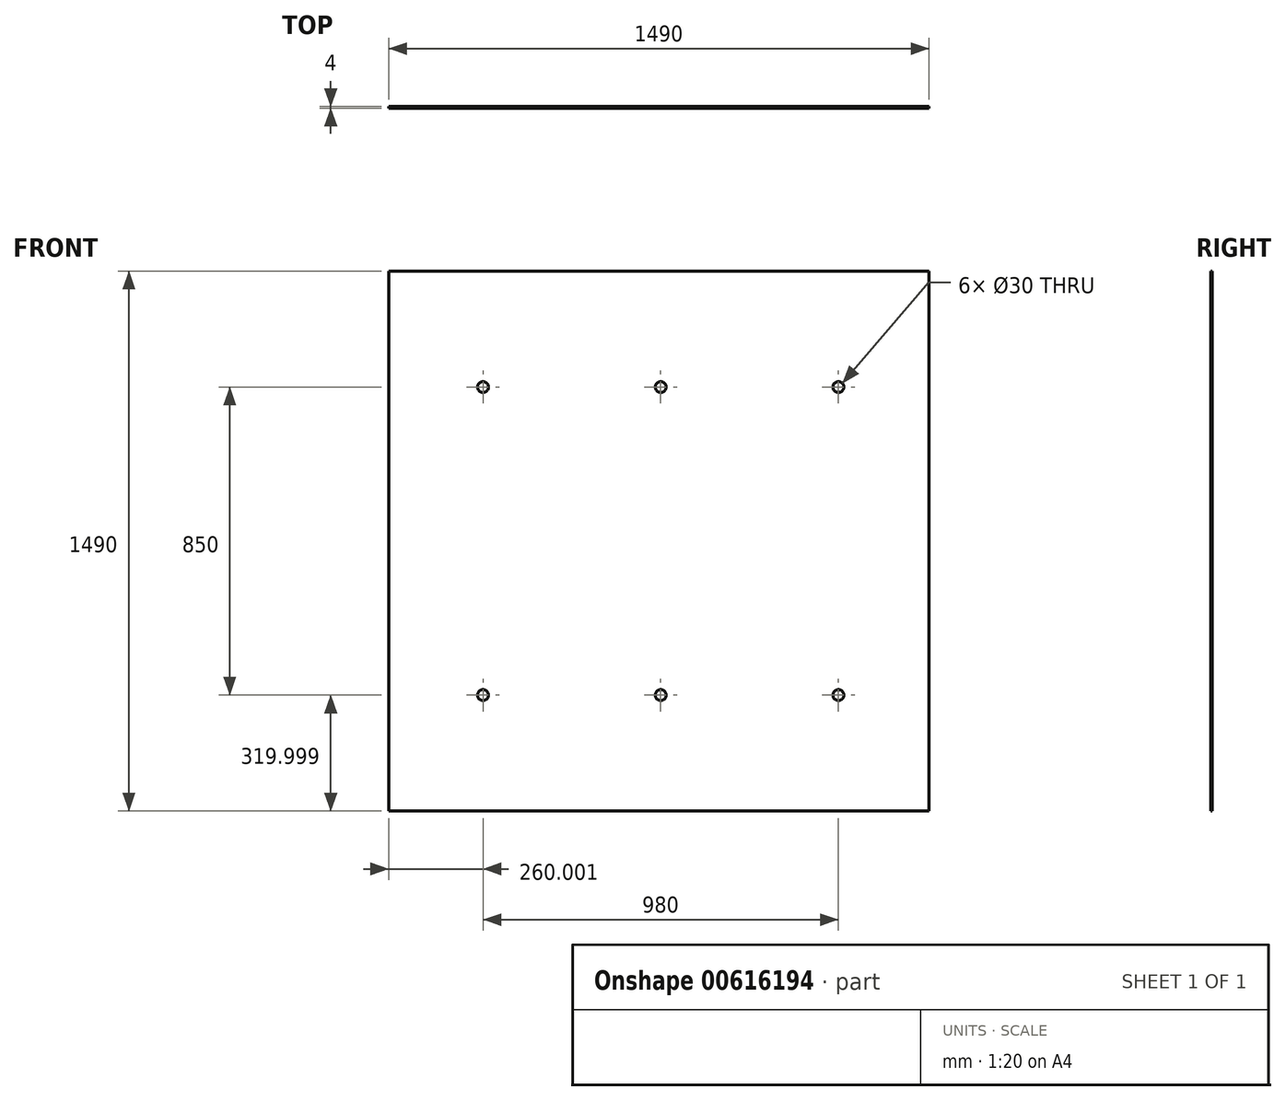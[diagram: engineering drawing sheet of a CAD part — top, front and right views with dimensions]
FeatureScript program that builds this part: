
annotation { "Feature Type Name" : "Feature", "Feature Type Description" : "" }
export const myFeature = defineFeature(function(context is Context, id is Id, definition is map)
    precondition{}
    {
        {
            var Q0;
            Q0=qCreatedBy(makeId("Front.planeOp"),FACE);
            var sketch = newSketch(context, id + "F0", { "sketchPlane" : qUnion([Q0])});
            skLineSegment(sketch, "E0.bottom", {"start": v(-98.39, 1446.63) * mm, "end": v(1391.61, 1446.63) * mm});
            skLineSegment(sketch, "E0.top", {"start": v(-98.39, -43.37) * mm, "end": v(1391.61, -43.37) * mm});
            skLineSegment(sketch, "E0.left", {"start": v(-98.39, 1446.63) * mm, "end": v(-98.39, -43.37) * mm});
            skLineSegment(sketch, "E0.right", {"start": v(1391.61, 1446.63) * mm, "end": v(1391.61, -43.37) * mm});
            skCircle(sketch, "E1", {"center": v(161.61, 1126.63) * mm, "radius": 15 * mm});
            skCircle(sketch, "E2.0.1.0", {"center": v(161.61, 276.63) * mm, "radius": 15 * mm});
            skCircle(sketch, "E2.1.0.0", {"center": v(651.61, 1126.63) * mm, "radius": 15 * mm});
            skCircle(sketch, "E2.1.1.0", {"center": v(651.61, 276.63) * mm, "radius": 15 * mm});
            skCircle(sketch, "E2.2.0.0", {"center": v(1141.61, 1126.63) * mm, "radius": 15 * mm});
            skCircle(sketch, "E2.2.1.0", {"center": v(1141.61, 276.63) * mm, "radius": 15 * mm});
            skLineSegment(sketch, "E2.direction1", {"start": v(161.61, 1126.63) * mm, "end": v(651.61, 1126.63) * mm, "construction": true});
            skLineSegment(sketch, "E2.direction2", {"start": v(161.61, 1126.63) * mm, "end": v(161.61, 276.63) * mm, "construction": true});
            skSolve(sketch);
        }
        {
            var Q0;
            Q0 = qSketchRegion(id + "F0", true);
            extrude(context, id + "F1", {"entities" : qUnion([Q0]), "depth" : 4 * mm, "offsetDistance" : 25 * mm});
        }
    });
